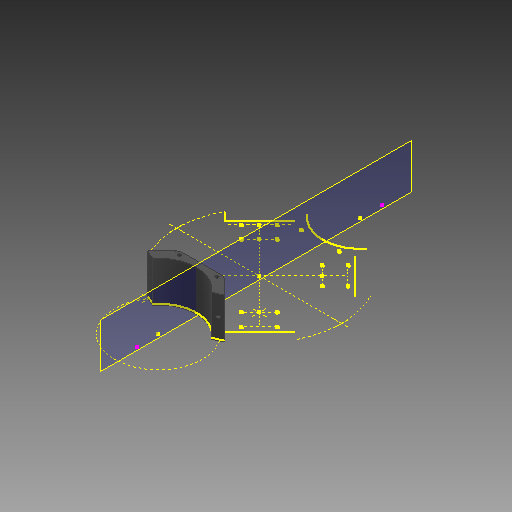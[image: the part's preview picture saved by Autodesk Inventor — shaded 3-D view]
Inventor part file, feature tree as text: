
AUTODESK INVENTOR PART (.ipt)
format: ipt  version: 2020 (Build 240168000, 168)  size: 177,152 bytes
history: native  units: mm
features: sketch x7, other x5, extrude x2, hole x2, fillet x1, mirror x1
ambient origin geometry x8: Origin, YZ Plane, XZ Plane, XY Plane, X Axis, Y Axis, Z Axis, Center Point
bodies: Body1 (feature_tree)
feature tree (18):
  other  "catch_v2"
  other  "floor_v2.ipt"
  other  "Твердое тело1"
  sketch  "Эскиз5"
  extrude  "Выдавливание1"  Depth=10.0mm
  hole  "Отверстие1"  [1 undecoded]
  hole  "Отверстие2"  [1 undecoded]
  fillet  "Сопряжение1"  Radius=51.15mm
  other  "РабПлоскость1"
  extrude  "Выдавливание2"  Depth=10.0mm
  other  "РабПлоскость2"
  mirror  "Зеркальное отражение1"
  sketch  "Эскиз2"
  sketch  "Эскиз3"
  sketch  "Эскиз6"
  sketch  "Эскиз8"
  sketch  "Эскиз9"
  sketch  "Эскиз10"
note: 2 required parameter values undecoded (feature->parameter linkage not recoverable at this tier; creation-order binding heuristic only, values carry confidence <= 0.55)
